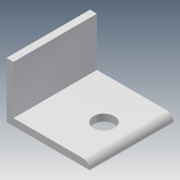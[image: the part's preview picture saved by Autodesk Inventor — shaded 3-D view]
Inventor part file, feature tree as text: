
AUTODESK INVENTOR PART (.ipt)
format: ipt  version: 2014 (Build 180170000, 170)  size: 97,280 bytes
history: native  units: in
note: dims shown in document units (in); Inventor stores cm internally (conversion verified against a paired STEP export)
features: extrude x3, sketch x3
ambient origin geometry x8: Origin, YZ Plane, XZ Plane, XY Plane, X Axis, Y Axis, Z Axis, Center Point
bodies: Solid1 (feature_tree)
feature tree (6):
  extrude  "Extrusion1"  Depth=1.5in
  extrude  "Extrusion2"  Depth=1.5in TaperAngle=0.0deg
  extrude  "Extrusion3"  Depth=1.5in
  sketch  "Sketch1"  dims[d0=1.5in d1=1.5in]
  sketch  "Sketch2"  dims[d2=0.125in d3=1.5in d4=0.0in]
  sketch  "Sketch3"  dims[d5=0.375in d6=0.5in d7=1.5in d8=0.0in d9=0.5in d10=1.5in d11=0.0in]
